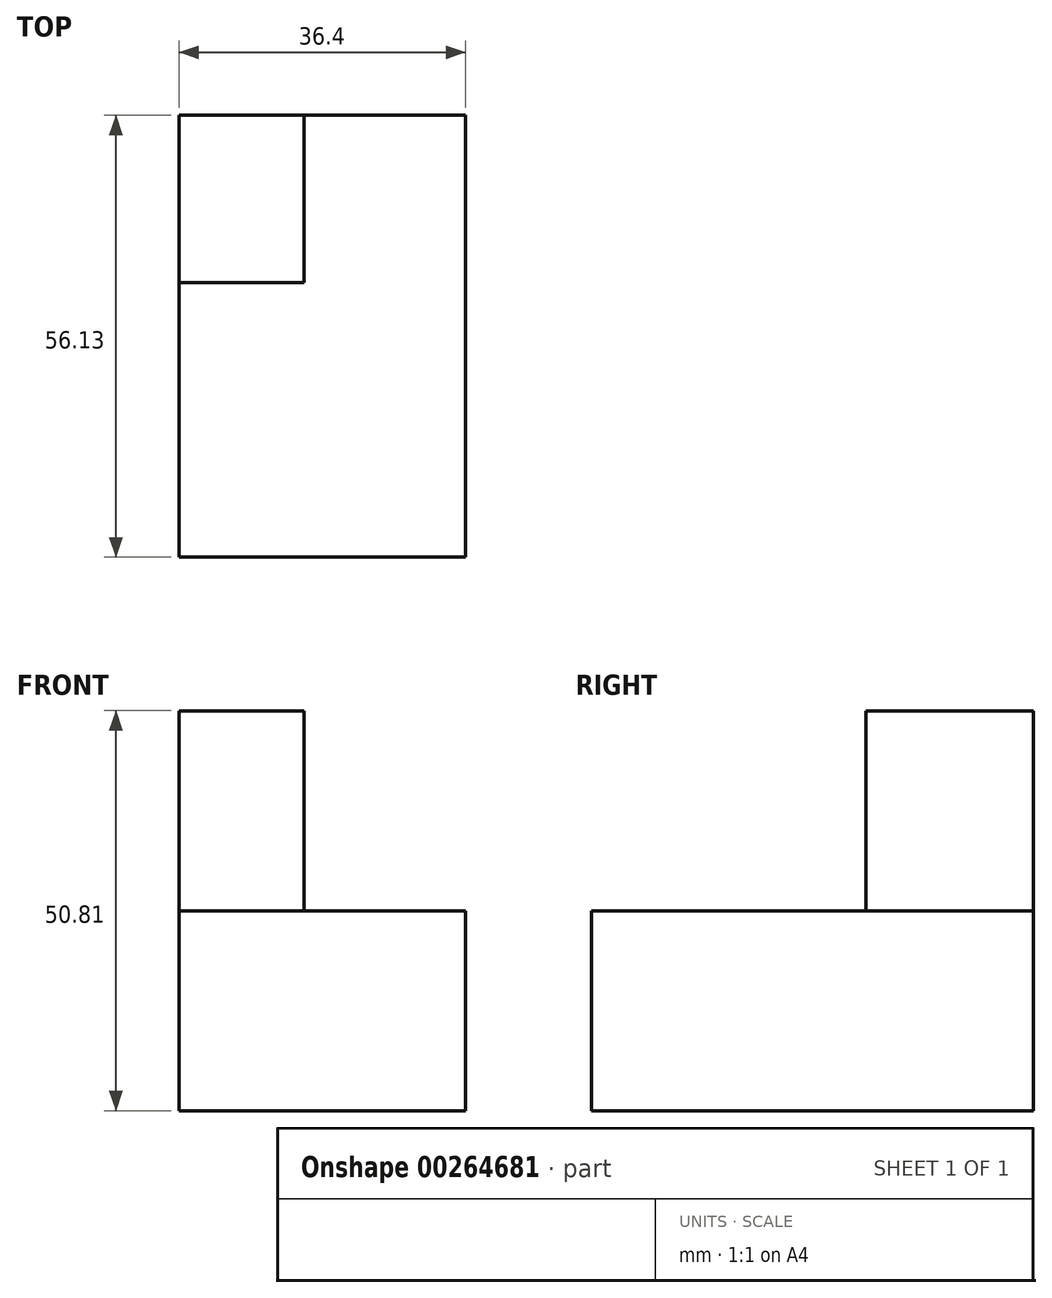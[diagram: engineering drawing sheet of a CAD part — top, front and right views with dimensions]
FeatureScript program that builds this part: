
annotation { "Feature Type Name" : "Feature", "Feature Type Description" : "" }
export const myFeature = defineFeature(function(context is Context, id is Id, definition is map)
    precondition{}
    {
        {
            var Q0;
            Q0=qCreatedBy(makeId("Front.planeOp"),FACE);
            var sketch = newSketch(context, id + "F0", { "sketchPlane" : qUnion([Q0])});
            skLineSegment(sketch, "E0.bottom", {"start": v(0, 0) * mm, "end": v(36.4, 0) * mm});
            skLineSegment(sketch, "E0.top", {"start": v(0, 25.4) * mm, "end": v(36.4, 25.4) * mm});
            skLineSegment(sketch, "E0.left", {"start": v(0, 0) * mm, "end": v(0, 25.4) * mm});
            skLineSegment(sketch, "E0.right", {"start": v(36.4, 0) * mm, "end": v(36.4, 25.4) * mm});
            skSolve(sketch);
        }
        {
            var Q0;
            Q0=makeQuery(id+"F0.imprint","IMPRINT",FACE,{"disambiguationData":[TD([[makeQuery(id+"F0.imprint","IMPRINT",EDGE,{"derivedFrom":sQuery(id+"F0.wireOp",EDGE,"E0.bottom")}),1.0]])]});
            extrude(context, id + "F1", {"entities" : qUnion([Q0]), "depth" : 56.13 * mm});
        }
        {
            var Q0;
            Q0=makeQuery(id+"F1.opExtrude","SWEPT_FACE",FACE,{"disambiguationData":[OSD([sQuery(id+"F0.wireOp",EDGE,"E0.top")])]});
            var sketch = newSketch(context, id + "F2", { "sketchPlane" : qUnion([Q0])});
            skLineSegment(sketch, "E1.bottom", {"start": v(0, 0) * mm, "end": v(15.93, 0) * mm});
            skLineSegment(sketch, "E1.top", {"start": v(0, -21.23) * mm, "end": v(15.93, -21.23) * mm});
            skLineSegment(sketch, "E1.left", {"start": v(0, 0) * mm, "end": v(0, -21.23) * mm});
            skLineSegment(sketch, "E1.right", {"start": v(15.93, 0) * mm, "end": v(15.93, -21.23) * mm});
            skSolve(sketch);
        }
        {
            var Q0;
            Q0=makeQuery(id+"F2.imprint","IMPRINT",FACE,{"disambiguationData":[TD([[makeQuery(id+"F2.imprint","IMPRINT",EDGE,{"derivedFrom":sQuery(id+"F2.wireOp",EDGE,"E1.bottom")}),-1.0]])]});
            extrude(context, id + "F3", {"entities" : qUnion([Q0]), "operationType" : NewBodyOperationType.ADD, "depth" : 25.4 * mm});
        }
    });
